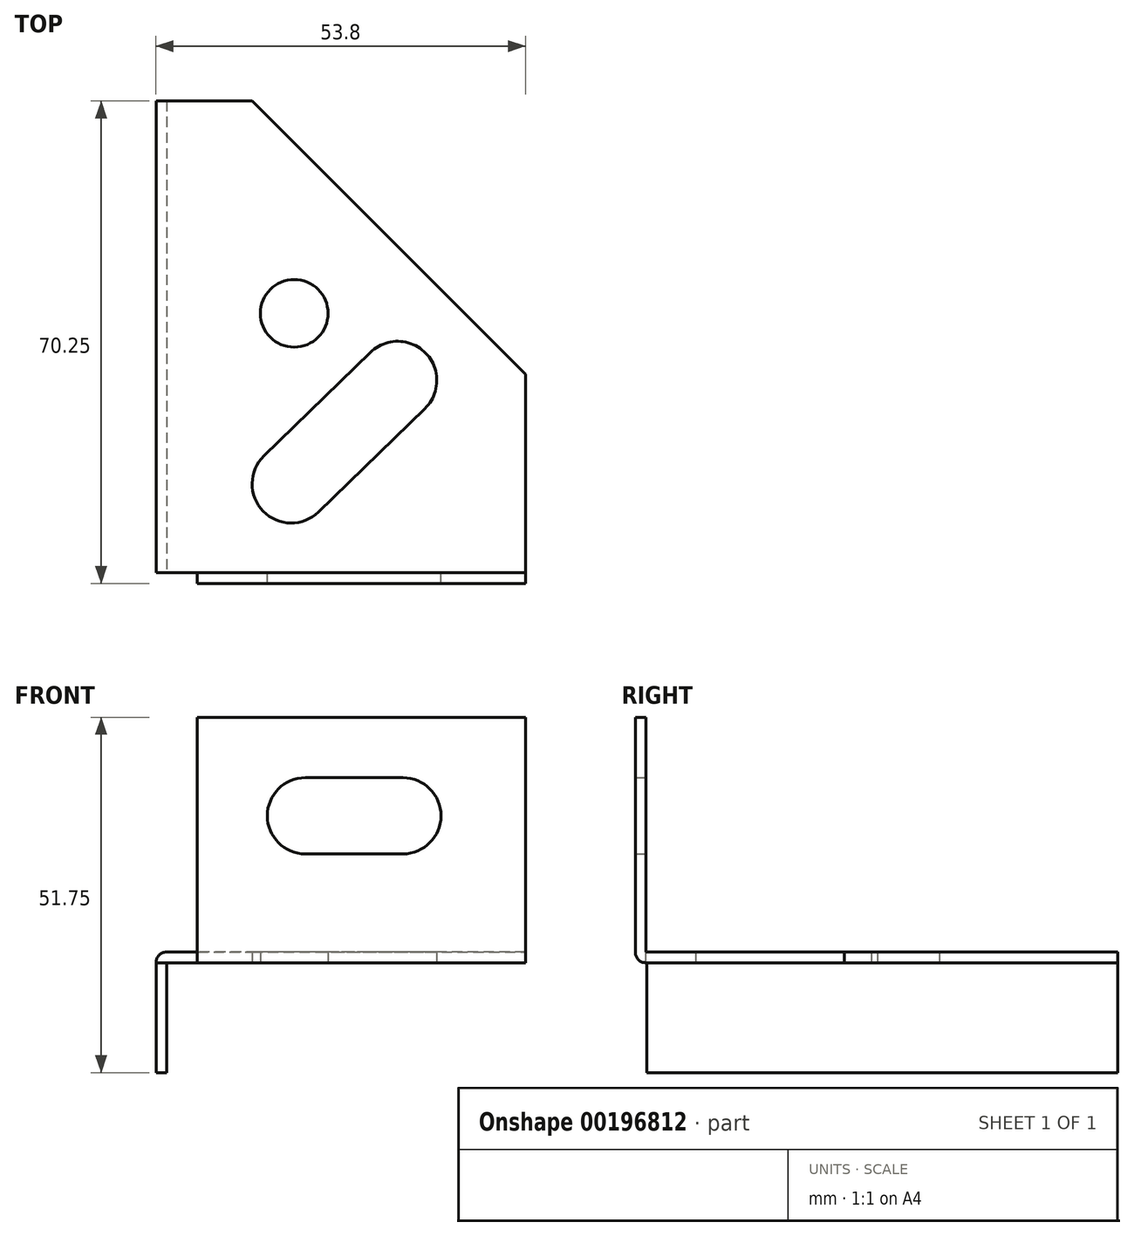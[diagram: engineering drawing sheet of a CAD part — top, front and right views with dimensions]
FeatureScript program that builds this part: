
annotation { "Feature Type Name" : "Feature", "Feature Type Description" : "" }
export const myFeature = defineFeature(function(context is Context, id is Id, definition is map)
    precondition{}
    {
        {
            var Q0;
            Q0=qCreatedBy(makeId("Top.planeOp"),FACE);
            var sketch = newSketch(context, id + "F0", { "sketchPlane" : qUnion([Q0])});
            skLineSegment(sketch, "E0", {"start": v(-51.36, -58.28) * mm, "end": v(2.44, -58.28) * mm});
            skLineSegment(sketch, "E1", {"start": v(2.44, -58.28) * mm, "end": v(2.44, -29.38) * mm});
            skLineSegment(sketch, "E2", {"start": v(-51.36, -58.28) * mm, "end": v(-51.36, 10.42) * mm});
            skLineSegment(sketch, "E3", {"start": v(-51.36, 10.42) * mm, "end": v(-37.36, 10.42) * mm});
            skLineSegment(sketch, "E4", {"start": v(-37.36, 10.42) * mm, "end": v(2.44, -29.38) * mm});
            skCircle(sketch, "E5", {"center": v(-31.23, -20.5) * mm, "radius": 4.92 * mm});
            skCircle(sketch, "E6", {"center": v(-31.66, -45.34) * mm, "radius": 5.7 * mm});
            skCircle(sketch, "E7", {"center": v(-16.17, -30.28) * mm, "radius": 5.7 * mm});
            skLineSegment(sketch, "E8", {"start": v(-20.15, -26.2) * mm, "end": v(-35.63, -41.25) * mm});
            skLineSegment(sketch, "E9", {"start": v(-27.68, -49.42) * mm, "end": v(-12.2, -34.36) * mm});
            skSolve(sketch);
        }
        {
            var Q0;
            Q0=makeQuery(id+"F0.imprint","IMPRINT",FACE,{"disambiguationData":[TD([[makeQuery(id+"F0.imprint","IMPRINT",EDGE,{"derivedFrom":sQuery(id+"F0.wireOp",EDGE,"E0")}),1.0]])]});
            extrude(context, id + "F1", {"entities" : qUnion([Q0]), "depth" : 1.55 * mm});
        }
        {
            var Q0;
            Q0=makeQuery(id+"F1.opExtrude","CAP_FACE",FACE,{"disambiguationData":[OSD([sQuery(id+"F0.wireOp",EDGE,"E0"),sQuery(id+"F0.wireOp",EDGE,"E1"),sQuery(id+"F0.wireOp",EDGE,"E2"),sQuery(id+"F0.wireOp",EDGE,"E3"),sQuery(id+"F0.wireOp",EDGE,"E4"),sQuery(id+"F0.wireOp",EDGE,"E5"),sQuery(id+"F0.wireOp",EDGE,"E6"),sQuery(id+"F0.wireOp",EDGE,"E7"),sQuery(id+"F0.wireOp",EDGE,"E8"),sQuery(id+"F0.wireOp",EDGE,"E9")])],"isStart":true});
            var sketch = newSketch(context, id + "F2", { "sketchPlane" : qUnion([Q0])});
            skLineSegment(sketch, "E10.bottom", {"start": v(-51.36, -10.42) * mm, "end": v(-49.8, -10.42) * mm});
            skLineSegment(sketch, "E10.top", {"start": v(-51.36, 58.18) * mm, "end": v(-49.8, 58.18) * mm});
            skLineSegment(sketch, "E10.left", {"start": v(-51.36, -10.42) * mm, "end": v(-51.36, 58.18) * mm});
            skLineSegment(sketch, "E10.right", {"start": v(-49.8, -10.42) * mm, "end": v(-49.8, 58.18) * mm});
            skSolve(sketch);
        }
        {
            var Q0;
            Q0=makeQuery(id+"F2.imprint","IMPRINT",FACE,{"disambiguationData":[TD([[makeQuery(id+"F2.imprint","IMPRINT",EDGE,{"derivedFrom":sQuery(id+"F2.wireOp",EDGE,"E10.bottom")}),1.0]])]});
            extrude(context, id + "F3", {"entities" : qUnion([Q0]), "operationType" : NewBodyOperationType.ADD, "depth" : 16 * mm});
        }
        {
            var Q0;
            Q0=makeQuery(id+"F1.opExtrude","CAP_FACE",FACE,{"disambiguationData":[OSD([sQuery(id+"F0.wireOp",EDGE,"E0"),sQuery(id+"F0.wireOp",EDGE,"E1"),sQuery(id+"F0.wireOp",EDGE,"E2"),sQuery(id+"F0.wireOp",EDGE,"E3"),sQuery(id+"F0.wireOp",EDGE,"E4"),sQuery(id+"F0.wireOp",EDGE,"E5"),sQuery(id+"F0.wireOp",EDGE,"E6"),sQuery(id+"F0.wireOp",EDGE,"E7"),sQuery(id+"F0.wireOp",EDGE,"E8"),sQuery(id+"F0.wireOp",EDGE,"E9")])],"isStart":false});
            var sketch = newSketch(context, id + "F4", { "sketchPlane" : qUnion([Q0])});
            skLineSegment(sketch, "E11.bottom", {"start": v(2.44, -58.28) * mm, "end": v(-45.36, -58.28) * mm});
            skLineSegment(sketch, "E11.top", {"start": v(2.44, -59.83) * mm, "end": v(-45.36, -59.83) * mm});
            skLineSegment(sketch, "E11.left", {"start": v(2.44, -58.28) * mm, "end": v(2.44, -59.83) * mm});
            skLineSegment(sketch, "E11.right", {"start": v(-45.36, -58.28) * mm, "end": v(-45.36, -59.83) * mm});
            skSolve(sketch);
        }
        {
            var Q0;
            Q0=makeQuery(id+"F4.imprint","IMPRINT",FACE,{"disambiguationData":[TD([[makeQuery(id+"F4.imprint","IMPRINT",EDGE,{"derivedFrom":sQuery(id+"F4.wireOp",EDGE,"E11.bottom")}),-1.0]])]});
            extrude(context, id + "F5", {"entities" : qUnion([Q0]), "operationType" : NewBodyOperationType.ADD, "oppositeDirection" : true, "depth" : 1.55 * mm});
        }
        {
            var Q0;
            Q0=makeQuery(id+"F5.boolean.opBoolean","MERGE",FACE,{"derivedFrom":[makeQuery(id+"F1.opExtrude","CAP_FACE",FACE,{"disambiguationData":[OSD([sQuery(id+"F0.wireOp",EDGE,"E0"),sQuery(id+"F0.wireOp",EDGE,"E1"),sQuery(id+"F0.wireOp",EDGE,"E2"),sQuery(id+"F0.wireOp",EDGE,"E3"),sQuery(id+"F0.wireOp",EDGE,"E4"),sQuery(id+"F0.wireOp",EDGE,"E5"),sQuery(id+"F0.wireOp",EDGE,"E6"),sQuery(id+"F0.wireOp",EDGE,"E7"),sQuery(id+"F0.wireOp",EDGE,"E8"),sQuery(id+"F0.wireOp",EDGE,"E9")])],"isStart":false}),makeQuery(id+"F5.opExtrude","CAP_FACE",FACE,{"disambiguationData":[OSD([sQuery(id+"F4.wireOp",EDGE,"E11.bottom"),sQuery(id+"F4.wireOp",EDGE,"E11.top"),sQuery(id+"F4.wireOp",EDGE,"E11.left"),sQuery(id+"F4.wireOp",EDGE,"E11.right")])],"isStart":true})]});
            var sketch = newSketch(context, id + "F6", { "sketchPlane" : qUnion([Q0])});
            skLineSegment(sketch, "E12.bottom", {"start": v(2.44, -59.83) * mm, "end": v(-45.36, -59.83) * mm});
            skLineSegment(sketch, "E12.top", {"start": v(2.44, -58.28) * mm, "end": v(-45.36, -58.28) * mm});
            skLineSegment(sketch, "E12.left", {"start": v(2.44, -59.83) * mm, "end": v(2.44, -58.28) * mm});
            skLineSegment(sketch, "E12.right", {"start": v(-45.36, -59.83) * mm, "end": v(-45.36, -58.28) * mm});
            skSolve(sketch);
        }
        {
            var Q0;
            Q0=makeQuery(id+"F6.imprint","IMPRINT",FACE,{"disambiguationData":[TD([[makeQuery(id+"F6.imprint","IMPRINT",EDGE,{"derivedFrom":sQuery(id+"F6.wireOp",EDGE,"E12.bottom")}),-1.0]])]});
            extrude(context, id + "F7", {"entities" : qUnion([Q0]), "operationType" : NewBodyOperationType.ADD, "depth" : 34.2 * mm});
        }
        {
            var Q0;
            Q0=makeQuery(id+"F5.opExtrude","CAP_EDGE",EDGE,{"disambiguationData":[OSD([sQuery(id+"F4.wireOp",EDGE,"E11.top")])],"isStart":false});
            var Q1;
            Q1=makeQuery(id+"F1.opExtrude","CAP_EDGE",EDGE,{"disambiguationData":[OSD([sQuery(id+"F0.wireOp",EDGE,"E2")])],"isStart":false});
            fillet(context, id + "F8", {"entities" : qUnion([Q0, Q1]), "radius" : 1.5 * mm, "tangentPropagation" : true, "allowEdgeOverflow" : false});
        }
        {
            var Q0;
            Q0=makeQuery(id+"F7.opExtrude","SWEPT_FACE",FACE,{"disambiguationData":[OSD([sQuery(id+"F6.wireOp",EDGE,"E12.top")])]});
            var sketch = newSketch(context, id + "F9", { "sketchPlane" : qUnion([Q0])});
            skCircle(sketch, "E13", {"center": v(15.4, 21.4) * mm, "radius": 5.55 * mm});
            skCircle(sketch, "E14", {"center": v(29.6, 21.4) * mm, "radius": 5.55 * mm});
            skLineSegment(sketch, "E15", {"start": v(15.4, 26.95) * mm, "end": v(29.6, 26.95) * mm});
            skLineSegment(sketch, "E16", {"start": v(15.4, 15.85) * mm, "end": v(29.6, 15.85) * mm});
            skSolve(sketch);
        }
        {
            var Q0;
            {var subQ0=sQuery(id+"F9.wireOp",EDGE,"E15");var subQ1=sQuery(id+"F9.wireOp",EDGE,"E13");var subQ2=makeQuery(id+"F9.imprint","INTERSECT",VERTEX,{"disambiguationData":[OD(0.0)],"derivedFrom":[subQ1,subQ0]});Q0=makeQuery(id+"F9.imprint","IMPRINT",FACE,{"disambiguationData":[TD([[makeQuery(id+"F9.imprint","IMPRINT",EDGE,{"disambiguationData":[TD([[subQ2,-1.0]])],"derivedFrom":subQ1}),1.0]])]});}
            var Q1;
            {var subQ0=sQuery(id+"F9.wireOp",EDGE,"E16");Q1=makeQuery(id+"F9.imprint","IMPRINT",FACE,{"disambiguationData":[TD([[makeQuery(id+"F9.imprint","IMPRINT",EDGE,{"derivedFrom":subQ0}),1.0]])]});}
            var Q2;
            {var subQ0=sQuery(id+"F9.wireOp",EDGE,"E14");var subQ1=makeQuery(id+"F9.imprint","INTERSECT",VERTEX,{"derivedFrom":[subQ0,sQuery(id+"F9.wireOp",EDGE,"E15")]});Q2=makeQuery(id+"F9.imprint","IMPRINT",FACE,{"disambiguationData":[TD([[makeQuery(id+"F9.imprint","IMPRINT",EDGE,{"disambiguationData":[TD([[subQ1,-1.0]])],"derivedFrom":subQ0}),1.0]])]});}
            extrude(context, id + "F10", {"entities" : qUnion([Q0, Q1, Q2]), "operationType" : NewBodyOperationType.REMOVE, "endBound" : BoundingType.THROUGH_ALL, "oppositeDirection" : true, "depth" : 25 * mm});
        }
    });
